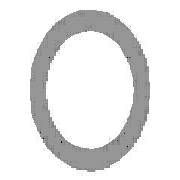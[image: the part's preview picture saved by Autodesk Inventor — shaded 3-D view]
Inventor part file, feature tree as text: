
AUTODESK INVENTOR PART (.ipt)
format: ipt  version: 2018 (Build 220112000, 112)  size: 138,240 bytes
history: native  units: mm (DEFAULTED — no unit token found)
features: plane x7, split x6, other x4, sketch x3
ambient origin geometry x8: Origin, YZ Plane, XZ Plane, XY Plane, X Axis, Y Axis, Z Axis, Center Point
bodies: Solid1 (feature_tree), Body (feature_tree)
feature tree (20):
  parser-record x1  (decoder bookkeeping rows leaked as tree rows — omitted from the tree; the rows remain in map.json)
  other  "Driven Length"
  other  "Start plane"
  other  "End plane"
  plane  "Work Plane4"
  split  "Split1"
  plane  "Work Plane5"
  split  "Split2"
  plane  "Work Plane6"
  split  "Split3"
  plane  "Work Plane7"
  split  "Split4"
  plane  "Work Plane8"
  split  "Split5"
  plane  "Work Plane9"
  split  "Split6"
  sketch  "Sketch"  dims[d2=262.853896mm d3=0.0mm d4=-21.486631mm d5=275.486631mm d6=90.0deg d7=296.973262mm]
  sketch  "Sketch3"  dims[d0=33.528mm]
  plane  "Work Plane3"
  sketch  "Sketch4"  dims[d1=3.3782mm]
